# Revit family: console with cutout for bowl with tap hole
name_source: partatom
category: Furniture
units: mm (PartAtom-declared; Revit-internal decimal feet)

## family parameters
Always vertical = Yes
Cut with Voids When Loaded = No
OmniClass Number = 23.21.19.15.33.13
Room Calculation Point = No
Shared = Yes
Work Plane-Based = No

## types (40) — shared parameters
BIMOBJECT = Sanitary: Compound units
CATALOG = Hansgrohe
DESIGN = Germany
ETIM = EC011381 | Bathroom furniture set
IFC = Furnishing element
L1 = 140
MASTERFORMAT = 12 35 30.23 | Bathroom Casework
Manufacturer = Hansgrohe
NBSYN = $BASENUMBER.-$ARTNR.-$SURFACE.-$LODLEVEL.
NN = Console with cutout for bowl with tap hole
OBJECTTYPE = Object (single object)
OMNICLASS = 23-19 31 17 11 | Bathroom Units
PRODUCTFAMILY = Xelu Q
PRODUCTGROUP = console
PRODUCTURL = https://pro.hansgrohe.com
REGIONSET = Worldwide
UNICLASS2015 = Pr_40_20_76_94 | Vanity units
UNIFORMATII = E2010 | Fixed Furnishings
UNSPSC = 56 | Furniture and Furnishings

## per-type parameters (varying)
| type | ARTNR | BASENUMBER | GTINCODE | L | LINA | LL | LODLEVEL | Model | NAME | NB | PERMALINK | SPECIFICATION | SURFACE | WEIGHT |
| Console 1180_550 with cutout in the middle for bowl with tap hole-54122050-GLOSSY_WHITE-200 | 54122050 | Console 1180/550 with cutout in the middle for bowl with tap hole | 4059625457979 | 1180 | Console 1180/550 with cutout in the middle for bowl with tap hole-54122050-GLOSSY_WHITE-200 | 590 | 200 | Console 1180/550 with cutout in the middle for bowl with tap hole-54122050-GLOSSY_WHITE-200 | Xelu Q Console 1180/550 with cutout in the middle for bowl with tap hole | Console 1180/550 with cutout in the middle for bowl with tap hole-54122050-GLOSSY_WHITE-200 | 54122XXX | Surfaces:    - 54122050 High Gloss White  - 54122910 Diamond Matt Grey  - 54122230 Natural Oak  - 54122630 Dark Walnut      Specification: | GLOSSY_WHITE | 14.5 |
| Console 1180_550 with cutout in the middle for bowl with tap hole-54122050-GLOSSY_WHITE-400 | 54122050 | Console 1180/550 with cutout in the middle for bowl with tap hole | 4059625457979 | 1180 | Console 1180/550 with cutout in the middle for bowl with tap hole-54122050-GLOSSY_WHITE-400 | 590 | 400 | Console 1180/550 with cutout in the middle for bowl with tap hole-54122050-GLOSSY_WHITE-400 | Xelu Q Console 1180/550 with cutout in the middle for bowl with tap hole | Console 1180/550 with cutout in the middle for bowl with tap hole-54122050-GLOSSY_WHITE-400 | 54122XXX | Surfaces:    - 54122050 High Gloss White  - 54122910 Diamond Matt Grey  - 54122230 Natural Oak  - 54122630 Dark Walnut      Specification: | GLOSSY_WHITE | 14.5 |
| Console 1180_550 with cutout in the middle for bowl with tap hole-54122230-NATURAL_OAK-200 | 54122230 | Console 1180/550 with cutout in the middle for bowl with tap hole | 4059625457979 | 1180 | Console 1180/550 with cutout in the middle for bowl with tap hole-54122230-NATURAL_OAK-200 | 590 | 200 | Console 1180/550 with cutout in the middle for bowl with tap hole-54122230-NATURAL_OAK-200 | Xelu Q Console 1180/550 with cutout in the middle for bowl with tap hole | Console 1180/550 with cutout in the middle for bowl with tap hole-54122230-NATURAL_OAK-200 | 54122XXX | Surfaces:    - 54122050 High Gloss White  - 54122910 Diamond Matt Grey  - 54122230 Natural Oak  - 54122630 Dark Walnut      Specification: | NATURAL_OAK | 14.5 |
| Console 1180_550 with cutout in the middle for bowl with tap hole-54122230-NATURAL_OAK-400 | 54122230 | Console 1180/550 with cutout in the middle for bowl with tap hole | 4059625457979 | 1180 | Console 1180/550 with cutout in the middle for bowl with tap hole-54122230-NATURAL_OAK-400 | 590 | 400 | Console 1180/550 with cutout in the middle for bowl with tap hole-54122230-NATURAL_OAK-400 | Xelu Q Console 1180/550 with cutout in the middle for bowl with tap hole | Console 1180/550 with cutout in the middle for bowl with tap hole-54122230-NATURAL_OAK-400 | 54122XXX | Surfaces:    - 54122050 High Gloss White  - 54122910 Diamond Matt Grey  - 54122230 Natural Oak  - 54122630 Dark Walnut      Specification: | NATURAL_OAK | 14.5 |
| Console 1180_550 with cutout in the middle for bowl with tap hole-54122630-DARK_WALNUT-200 | 54122630 | Console 1180/550 with cutout in the middle for bowl with tap hole | 4059625457979 | 1180 | Console 1180/550 with cutout in the middle for bowl with tap hole-54122630-DARK_WALNUT-200 | 590 | 200 | Console 1180/550 with cutout in the middle for bowl with tap hole-54122630-DARK_WALNUT-200 | Xelu Q Console 1180/550 with cutout in the middle for bowl with tap hole | Console 1180/550 with cutout in the middle for bowl with tap hole-54122630-DARK_WALNUT-200 | 54122XXX | Surfaces:    - 54122050 High Gloss White  - 54122910 Diamond Matt Grey  - 54122230 Natural Oak  - 54122630 Dark Walnut      Specification: | DARK_WALNUT | 14.5 |
| Console 1180_550 with cutout in the middle for bowl with tap hole-54122630-DARK_WALNUT-400 | 54122630 | Console 1180/550 with cutout in the middle for bowl with tap hole | 4059625457979 | 1180 | Console 1180/550 with cutout in the middle for bowl with tap hole-54122630-DARK_WALNUT-400 | 590 | 400 | Console 1180/550 with cutout in the middle for bowl with tap hole-54122630-DARK_WALNUT-400 | Xelu Q Console 1180/550 with cutout in the middle for bowl with tap hole | Console 1180/550 with cutout in the middle for bowl with tap hole-54122630-DARK_WALNUT-400 | 54122XXX | Surfaces:    - 54122050 High Gloss White  - 54122910 Diamond Matt Grey  - 54122230 Natural Oak  - 54122630 Dark Walnut      Specification: | DARK_WALNUT | 14.5 |
| Console 1180_550 with cutout in the middle for bowl with tap hole-54122910-DIAMOND_GREY-200 | 54122910 | Console 1180/550 with cutout in the middle for bowl with tap hole | 4059625457979 | 1180 | Console 1180/550 with cutout in the middle for bowl with tap hole-54122910-DIAMOND_GREY-200 | 590 | 200 | Console 1180/550 with cutout in the middle for bowl with tap hole-54122910-DIAMOND_GREY-200 | Xelu Q Console 1180/550 with cutout in the middle for bowl with tap hole | Console 1180/550 with cutout in the middle for bowl with tap hole-54122910-DIAMOND_GREY-200 | 54122XXX | Surfaces:    - 54122050 High Gloss White  - 54122910 Diamond Matt Grey  - 54122230 Natural Oak  - 54122630 Dark Walnut      Specification: | DIAMOND_GREY | 14.5 |
| Console 1180_550 with cutout in the middle for bowl with tap hole-54122910-DIAMOND_GREY-400 | 54122910 | Console 1180/550 with cutout in the middle for bowl with tap hole | 4059625457979 | 1180 | Console 1180/550 with cutout in the middle for bowl with tap hole-54122910-DIAMOND_GREY-400 | 590 | 400 | Console 1180/550 with cutout in the middle for bowl with tap hole-54122910-DIAMOND_GREY-400 | Xelu Q Console 1180/550 with cutout in the middle for bowl with tap hole | Console 1180/550 with cutout in the middle for bowl with tap hole-54122910-DIAMOND_GREY-400 | 54122XXX | Surfaces:    - 54122050 High Gloss White  - 54122910 Diamond Matt Grey  - 54122230 Natural Oak  - 54122630 Dark Walnut      Specification: | DIAMOND_GREY | 14.5 |
| Console 1360_550 with cutout left for bowl with tap hole-54123050-GLOSSY_WHITE-200 | 54123050 | Console 1360/550 with cutout left for bowl with tap hole | 4059625457931 | 1360 | Console 1360/550 with cutout left for bowl with tap hole-54123050-GLOSSY_WHITE-200 | 340 | 200 | Console 1360/550 with cutout left for bowl with tap hole-54123050-GLOSSY_WHITE-200 | Xelu Q Console 1360/550 with cutout left for bowl with tap hole | Console 1360/550 with cutout left for bowl with tap hole-54123050-GLOSSY_WHITE-200 | 54123XXX | Surfaces:    - 54123050 High Gloss White  - 54123910 Diamond Matt Grey  - 54123230 Natural Oak  - 54123630 Dark Walnut      Specification: | GLOSSY_WHITE | 12.2 |
| Console 1360_550 with cutout left for bowl with tap hole-54123050-GLOSSY_WHITE-400 | 54123050 | Console 1360/550 with cutout left for bowl with tap hole | 4059625457931 | 1360 | Console 1360/550 with cutout left for bowl with tap hole-54123050-GLOSSY_WHITE-400 | 340 | 400 | Console 1360/550 with cutout left for bowl with tap hole-54123050-GLOSSY_WHITE-400 | Xelu Q Console 1360/550 with cutout left for bowl with tap hole | Console 1360/550 with cutout left for bowl with tap hole-54123050-GLOSSY_WHITE-400 | 54123XXX | Surfaces:    - 54123050 High Gloss White  - 54123910 Diamond Matt Grey  - 54123230 Natural Oak  - 54123630 Dark Walnut      Specification: | GLOSSY_WHITE | 12.2 |
| Console 1360_550 with cutout left for bowl with tap hole-54123230-NATURAL_OAK-200 | 54123230 | Console 1360/550 with cutout left for bowl with tap hole | 4059625457931 | 1360 | Console 1360/550 with cutout left for bowl with tap hole-54123230-NATURAL_OAK-200 | 340 | 200 | Console 1360/550 with cutout left for bowl with tap hole-54123230-NATURAL_OAK-200 | Xelu Q Console 1360/550 with cutout left for bowl with tap hole | Console 1360/550 with cutout left for bowl with tap hole-54123230-NATURAL_OAK-200 | 54123XXX | Surfaces:    - 54123050 High Gloss White  - 54123910 Diamond Matt Grey  - 54123230 Natural Oak  - 54123630 Dark Walnut      Specification: | NATURAL_OAK | 12.2 |
| Console 1360_550 with cutout left for bowl with tap hole-54123230-NATURAL_OAK-400 | 54123230 | Console 1360/550 with cutout left for bowl with tap hole | 4059625457931 | 1360 | Console 1360/550 with cutout left for bowl with tap hole-54123230-NATURAL_OAK-400 | 340 | 400 | Console 1360/550 with cutout left for bowl with tap hole-54123230-NATURAL_OAK-400 | Xelu Q Console 1360/550 with cutout left for bowl with tap hole | Console 1360/550 with cutout left for bowl with tap hole-54123230-NATURAL_OAK-400 | 54123XXX | Surfaces:    - 54123050 High Gloss White  - 54123910 Diamond Matt Grey  - 54123230 Natural Oak  - 54123630 Dark Walnut      Specification: | NATURAL_OAK | 12.2 |
| Console 1360_550 with cutout left for bowl with tap hole-54123630-DIAMOND_GREY-200 | 54123630 | Console 1360/550 with cutout left for bowl with tap hole | 4059625457931 | 1360 | Console 1360/550 with cutout left for bowl with tap hole-54123630-DIAMOND_GREY-200 | 340 | 200 | Console 1360/550 with cutout left for bowl with tap hole-54123630-DIAMOND_GREY-200 | Xelu Q Console 1360/550 with cutout left for bowl with tap hole | Console 1360/550 with cutout left for bowl with tap hole-54123630-DIAMOND_GREY-200 | 54123XXX | Surfaces:    - 54123050 High Gloss White  - 54123910 Diamond Matt Grey  - 54123230 Natural Oak  - 54123630 Dark Walnut      Specification: | DIAMOND_GREY | 12.2 |
| Console 1360_550 with cutout left for bowl with tap hole-54123630-DIAMOND_GREY-400 | 54123630 | Console 1360/550 with cutout left for bowl with tap hole | 4059625457931 | 1360 | Console 1360/550 with cutout left for bowl with tap hole-54123630-DIAMOND_GREY-400 | 340 | 400 | Console 1360/550 with cutout left for bowl with tap hole-54123630-DIAMOND_GREY-400 | Xelu Q Console 1360/550 with cutout left for bowl with tap hole | Console 1360/550 with cutout left for bowl with tap hole-54123630-DIAMOND_GREY-400 | 54123XXX | Surfaces:    - 54123050 High Gloss White  - 54123910 Diamond Matt Grey  - 54123230 Natural Oak  - 54123630 Dark Walnut      Specification: | DIAMOND_GREY | 12.2 |
| Console 1360_550 with cutout left for bowl with tap hole-54123910-DARK_WALNUT-200 | 54123910 | Console 1360/550 with cutout left for bowl with tap hole | 4059625457931 | 1360 | Console 1360/550 with cutout left for bowl with tap hole-54123910-DARK_WALNUT-200 | 340 | 200 | Console 1360/550 with cutout left for bowl with tap hole-54123910-DARK_WALNUT-200 | Xelu Q Console 1360/550 with cutout left for bowl with tap hole | Console 1360/550 with cutout left for bowl with tap hole-54123910-DARK_WALNUT-200 | 54123XXX | Surfaces:    - 54123050 High Gloss White  - 54123910 Diamond Matt Grey  - 54123230 Natural Oak  - 54123630 Dark Walnut      Specification: | DARK_WALNUT | 12.2 |
| Console 1360_550 with cutout left for bowl with tap hole-54123910-DARK_WALNUT-400 | 54123910 | Console 1360/550 with cutout left for bowl with tap hole | 4059625457931 | 1360 | Console 1360/550 with cutout left for bowl with tap hole-54123910-DARK_WALNUT-400 | 340 | 400 | Console 1360/550 with cutout left for bowl with tap hole-54123910-DARK_WALNUT-400 | Xelu Q Console 1360/550 with cutout left for bowl with tap hole | Console 1360/550 with cutout left for bowl with tap hole-54123910-DARK_WALNUT-400 | 54123XXX | Surfaces:    - 54123050 High Gloss White  - 54123910 Diamond Matt Grey  - 54123230 Natural Oak  - 54123630 Dark Walnut      Specification: | DARK_WALNUT | 12.2 |
| Console 1360_550 with cutout right for bowl with tap hole-54124050-NATURAL_OAK-200 | 54124050 | Console 1360/550 with cutout right for bowl with tap hole | 4059625457894 | 1360 | Console 1360/550 with cutout right for bowl with tap hole-54124050-NATURAL_OAK-200 | 1020 | 200 | Console 1360/550 with cutout right for bowl with tap hole-54124050-NATURAL_OAK-200 | Xelu Q Console 1360/550 with cutout right for bowl with tap hole | Console 1360/550 with cutout right for bowl with tap hole-54124050-NATURAL_OAK-200 | 54124XXX | Surfaces:    - 54124050 High Gloss White  - 54124910 Diamond Matt Grey  - 54124230 Natural Oak  - 54124630 Dark Walnut      Specification: | NATURAL_OAK | 12.2 |
| Console 1360_550 with cutout right for bowl with tap hole-54124050-NATURAL_OAK-400 | 54124050 | Console 1360/550 with cutout right for bowl with tap hole | 4059625457894 | 1360 | Console 1360/550 with cutout right for bowl with tap hole-54124050-NATURAL_OAK-400 | 1020 | 400 | Console 1360/550 with cutout right for bowl with tap hole-54124050-NATURAL_OAK-400 | Xelu Q Console 1360/550 with cutout right for bowl with tap hole | Console 1360/550 with cutout right for bowl with tap hole-54124050-NATURAL_OAK-400 | 54124XXX | Surfaces:    - 54124050 High Gloss White  - 54124910 Diamond Matt Grey  - 54124230 Natural Oak  - 54124630 Dark Walnut      Specification: | NATURAL_OAK | 12.2 |
| Console 1360_550 with cutout right for bowl with tap hole-54124230-DIAMOND_GREY-200 | 54124230 | Console 1360/550 with cutout right for bowl with tap hole | 4059625457894 | 1360 | Console 1360/550 with cutout right for bowl with tap hole-54124230-DIAMOND_GREY-200 | 1020 | 200 | Console 1360/550 with cutout right for bowl with tap hole-54124230-DIAMOND_GREY-200 | Xelu Q Console 1360/550 with cutout right for bowl with tap hole | Console 1360/550 with cutout right for bowl with tap hole-54124230-DIAMOND_GREY-200 | 54124XXX | Surfaces:    - 54124050 High Gloss White  - 54124910 Diamond Matt Grey  - 54124230 Natural Oak  - 54124630 Dark Walnut      Specification: | DIAMOND_GREY | 12.2 |
| Console 1360_550 with cutout right for bowl with tap hole-54124230-DIAMOND_GREY-400 | 54124230 | Console 1360/550 with cutout right for bowl with tap hole | 4059625457894 | 1360 | Console 1360/550 with cutout right for bowl with tap hole-54124230-DIAMOND_GREY-400 | 1020 | 400 | Console 1360/550 with cutout right for bowl with tap hole-54124230-DIAMOND_GREY-400 | Xelu Q Console 1360/550 with cutout right for bowl with tap hole | Console 1360/550 with cutout right for bowl with tap hole-54124230-DIAMOND_GREY-400 | 54124XXX | Surfaces:    - 54124050 High Gloss White  - 54124910 Diamond Matt Grey  - 54124230 Natural Oak  - 54124630 Dark Walnut      Specification: | DIAMOND_GREY | 12.2 |
| Console 1360_550 with cutout right for bowl with tap hole-54124630-DARK_WALNUT-200 | 54124630 | Console 1360/550 with cutout right for bowl with tap hole | 4059625457894 | 1360 | Console 1360/550 with cutout right for bowl with tap hole-54124630-DARK_WALNUT-200 | 1020 | 200 | Console 1360/550 with cutout right for bowl with tap hole-54124630-DARK_WALNUT-200 | Xelu Q Console 1360/550 with cutout right for bowl with tap hole | Console 1360/550 with cutout right for bowl with tap hole-54124630-DARK_WALNUT-200 | 54124XXX | Surfaces:    - 54124050 High Gloss White  - 54124910 Diamond Matt Grey  - 54124230 Natural Oak  - 54124630 Dark Walnut      Specification: | DARK_WALNUT | 12.2 |
| Console 1360_550 with cutout right for bowl with tap hole-54124630-DARK_WALNUT-400 | 54124630 | Console 1360/550 with cutout right for bowl with tap hole | 4059625457894 | 1360 | Console 1360/550 with cutout right for bowl with tap hole-54124630-DARK_WALNUT-400 | 1020 | 400 | Console 1360/550 with cutout right for bowl with tap hole-54124630-DARK_WALNUT-400 | Xelu Q Console 1360/550 with cutout right for bowl with tap hole | Console 1360/550 with cutout right for bowl with tap hole-54124630-DARK_WALNUT-400 | 54124XXX | Surfaces:    - 54124050 High Gloss White  - 54124910 Diamond Matt Grey  - 54124230 Natural Oak  - 54124630 Dark Walnut      Specification: | DARK_WALNUT | 12.2 |
| Console 1360_550 with cutout right for bowl with tap hole-54124910-GLOSSY_WHITE-200 | 54124910 | Console 1360/550 with cutout right for bowl with tap hole | 4059625457894 | 1360 | Console 1360/550 with cutout right for bowl with tap hole-54124910-GLOSSY_WHITE-200 | 1020 | 200 | Console 1360/550 with cutout right for bowl with tap hole-54124910-GLOSSY_WHITE-200 | Xelu Q Console 1360/550 with cutout right for bowl with tap hole | Console 1360/550 with cutout right for bowl with tap hole-54124910-GLOSSY_WHITE-200 | 54124XXX | Surfaces:    - 54124050 High Gloss White  - 54124910 Diamond Matt Grey  - 54124230 Natural Oak  - 54124630 Dark Walnut      Specification: | GLOSSY_WHITE | 12.2 |
| Console 1360_550 with cutout right for bowl with tap hole-54124910-GLOSSY_WHITE-400 | 54124910 | Console 1360/550 with cutout right for bowl with tap hole | 4059625457894 | 1360 | Console 1360/550 with cutout right for bowl with tap hole-54124910-GLOSSY_WHITE-400 | 1020 | 400 | Console 1360/550 with cutout right for bowl with tap hole-54124910-GLOSSY_WHITE-400 | Xelu Q Console 1360/550 with cutout right for bowl with tap hole | Console 1360/550 with cutout right for bowl with tap hole-54124910-GLOSSY_WHITE-400 | 54124XXX | Surfaces:    - 54124050 High Gloss White  - 54124910 Diamond Matt Grey  - 54124230 Natural Oak  - 54124630 Dark Walnut      Specification: | GLOSSY_WHITE | 12.2 |
| Console 780_550 with cutout in the middle for bowls with tap hole-54120050-DARK_WALNUT-200 | 54120050 | Console 780/550 with cutout in the middle for bowls with tap hole | 4059625457658 | 780 | Console 780/550 with cutout in the middle for bowls with tap hole-54120050-DARK_WALNUT-200 | 390 | 200 | Console 780/550 with cutout in the middle for bowls with tap hole-54120050-DARK_WALNUT-200 | Xelu Q Console 780/550 with cutout in the middle for bowls with tap hole | Console 780/550 with cutout in the middle for bowls with tap hole-54120050-DARK_WALNUT-200 | 54120XXX | Surfaces:    - 54120050 High Gloss White  - 54120910 Diamond Matt Grey  - 54120230 Natural Oak  - 54120630 Dark Walnut      Specification: | DARK_WALNUT | 8.4 |
| Console 780_550 with cutout in the middle for bowls with tap hole-54120050-DARK_WALNUT-400 | 54120050 | Console 780/550 with cutout in the middle for bowls with tap hole | 4059625457658 | 780 | Console 780/550 with cutout in the middle for bowls with tap hole-54120050-DARK_WALNUT-400 | 390 | 400 | Console 780/550 with cutout in the middle for bowls with tap hole-54120050-DARK_WALNUT-400 | Xelu Q Console 780/550 with cutout in the middle for bowls with tap hole | Console 780/550 with cutout in the middle for bowls with tap hole-54120050-DARK_WALNUT-400 | 54120XXX | Surfaces:    - 54120050 High Gloss White  - 54120910 Diamond Matt Grey  - 54120230 Natural Oak  - 54120630 Dark Walnut      Specification: | DARK_WALNUT | 8.4 |
| Console 780_550 with cutout in the middle for bowls with tap hole-54120230-DIAMOND_GREY-200 | 54120230 | Console 780/550 with cutout in the middle for bowls with tap hole | 4059625457658 | 780 | Console 780/550 with cutout in the middle for bowls with tap hole-54120230-DIAMOND_GREY-200 | 390 | 200 | Console 780/550 with cutout in the middle for bowls with tap hole-54120230-DIAMOND_GREY-200 | Xelu Q Console 780/550 with cutout in the middle for bowls with tap hole | Console 780/550 with cutout in the middle for bowls with tap hole-54120230-DIAMOND_GREY-200 | 54120XXX | Surfaces:    - 54120050 High Gloss White  - 54120910 Diamond Matt Grey  - 54120230 Natural Oak  - 54120630 Dark Walnut      Specification: | DIAMOND_GREY | 8.4 |
| Console 780_550 with cutout in the middle for bowls with tap hole-54120230-DIAMOND_GREY-400 | 54120230 | Console 780/550 with cutout in the middle for bowls with tap hole | 4059625457658 | 780 | Console 780/550 with cutout in the middle for bowls with tap hole-54120230-DIAMOND_GREY-400 | 390 | 400 | Console 780/550 with cutout in the middle for bowls with tap hole-54120230-DIAMOND_GREY-400 | Xelu Q Console 780/550 with cutout in the middle for bowls with tap hole | Console 780/550 with cutout in the middle for bowls with tap hole-54120230-DIAMOND_GREY-400 | 54120XXX | Surfaces:    - 54120050 High Gloss White  - 54120910 Diamond Matt Grey  - 54120230 Natural Oak  - 54120630 Dark Walnut      Specification: | DIAMOND_GREY | 8.4 |
| Console 780_550 with cutout in the middle for bowls with tap hole-54120630-NATURAL_OAK-200 | 54120630 | Console 780/550 with cutout in the middle for bowls with tap hole | 4059625457658 | 780 | Console 780/550 with cutout in the middle for bowls with tap hole-54120630-NATURAL_OAK-200 | 390 | 200 | Console 780/550 with cutout in the middle for bowls with tap hole-54120630-NATURAL_OAK-200 | Xelu Q Console 780/550 with cutout in the middle for bowls with tap hole | Console 780/550 with cutout in the middle for bowls with tap hole-54120630-NATURAL_OAK-200 | 54120XXX | Surfaces:    - 54120050 High Gloss White  - 54120910 Diamond Matt Grey  - 54120230 Natural Oak  - 54120630 Dark Walnut      Specification: | NATURAL_OAK | 8.4 |
| Console 780_550 with cutout in the middle for bowls with tap hole-54120630-NATURAL_OAK-400 | 54120630 | Console 780/550 with cutout in the middle for bowls with tap hole | 4059625457658 | 780 | Console 780/550 with cutout in the middle for bowls with tap hole-54120630-NATURAL_OAK-400 | 390 | 400 | Console 780/550 with cutout in the middle for bowls with tap hole-54120630-NATURAL_OAK-400 | Xelu Q Console 780/550 with cutout in the middle for bowls with tap hole | Console 780/550 with cutout in the middle for bowls with tap hole-54120630-NATURAL_OAK-400 | 54120XXX | Surfaces:    - 54120050 High Gloss White  - 54120910 Diamond Matt Grey  - 54120230 Natural Oak  - 54120630 Dark Walnut      Specification: | NATURAL_OAK | 8.4 |
| Console 780_550 with cutout in the middle for bowls with tap hole-54120910-GLOSSY_WHITE-200 | 54120910 | Console 780/550 with cutout in the middle for bowls with tap hole | 4059625457658 | 780 | Console 780/550 with cutout in the middle for bowls with tap hole-54120910-GLOSSY_WHITE-200 | 390 | 200 | Console 780/550 with cutout in the middle for bowls with tap hole-54120910-GLOSSY_WHITE-200 | Xelu Q Console 780/550 with cutout in the middle for bowls with tap hole | Console 780/550 with cutout in the middle for bowls with tap hole-54120910-GLOSSY_WHITE-200 | 54120XXX | Surfaces:    - 54120050 High Gloss White  - 54120910 Diamond Matt Grey  - 54120230 Natural Oak  - 54120630 Dark Walnut      Specification: | GLOSSY_WHITE | 8.4 |
| Console 780_550 with cutout in the middle for bowls with tap hole-54120910-GLOSSY_WHITE-400 | 54120910 | Console 780/550 with cutout in the middle for bowls with tap hole | 4059625457658 | 780 | Console 780/550 with cutout in the middle for bowls with tap hole-54120910-GLOSSY_WHITE-400 | 390 | 400 | Console 780/550 with cutout in the middle for bowls with tap hole-54120910-GLOSSY_WHITE-400 | Xelu Q Console 780/550 with cutout in the middle for bowls with tap hole | Console 780/550 with cutout in the middle for bowls with tap hole-54120910-GLOSSY_WHITE-400 | 54120XXX | Surfaces:    - 54120050 High Gloss White  - 54120910 Diamond Matt Grey  - 54120230 Natural Oak  - 54120630 Dark Walnut      Specification: | GLOSSY_WHITE | 8.4 |
| Console 980_550 with cutout in the middle for bowl with tap hole-54121050-NATURAL_OAK-200 | 54121050 | Console 980/550 with cutout in the middle for bowl with tap hole | 4059625458013 | 980 | Console 980/550 with cutout in the middle for bowl with tap hole-54121050-NATURAL_OAK-200 | 490 | 200 | Console 980/550 with cutout in the middle for bowl with tap hole-54121050-NATURAL_OAK-200 | Xelu Q Console 980/550 with cutout in the middle for bowl with tap hole | Console 980/550 with cutout in the middle for bowl with tap hole-54121050-NATURAL_OAK-200 | 54121XXX | Surfaces:    - 54121050 High Gloss White  - 54121910 Diamond Matt Grey  - 54121230 Natural Oak  - 54121630 Dark Walnut      Specification: | NATURAL_OAK | 13.2 |
| Console 980_550 with cutout in the middle for bowl with tap hole-54121050-NATURAL_OAK-400 | 54121050 | Console 980/550 with cutout in the middle for bowl with tap hole | 4059625458013 | 980 | Console 980/550 with cutout in the middle for bowl with tap hole-54121050-NATURAL_OAK-400 | 490 | 400 | Console 980/550 with cutout in the middle for bowl with tap hole-54121050-NATURAL_OAK-400 | Xelu Q Console 980/550 with cutout in the middle for bowl with tap hole | Console 980/550 with cutout in the middle for bowl with tap hole-54121050-NATURAL_OAK-400 | 54121XXX | Surfaces:    - 54121050 High Gloss White  - 54121910 Diamond Matt Grey  - 54121230 Natural Oak  - 54121630 Dark Walnut      Specification: | NATURAL_OAK | 13.2 |
| Console 980_550 with cutout in the middle for bowl with tap hole-54121230-GLOSSY_WHITE-200 | 54121230 | Console 980/550 with cutout in the middle for bowl with tap hole | 4059625458013 | 980 | Console 980/550 with cutout in the middle for bowl with tap hole-54121230-GLOSSY_WHITE-200 | 490 | 200 | Console 980/550 with cutout in the middle for bowl with tap hole-54121230-GLOSSY_WHITE-200 | Xelu Q Console 980/550 with cutout in the middle for bowl with tap hole | Console 980/550 with cutout in the middle for bowl with tap hole-54121230-GLOSSY_WHITE-200 | 54121XXX | Surfaces:    - 54121050 High Gloss White  - 54121910 Diamond Matt Grey  - 54121230 Natural Oak  - 54121630 Dark Walnut      Specification: | GLOSSY_WHITE | 13.2 |
| Console 980_550 with cutout in the middle for bowl with tap hole-54121230-GLOSSY_WHITE-400 | 54121230 | Console 980/550 with cutout in the middle for bowl with tap hole | 4059625458013 | 980 | Console 980/550 with cutout in the middle for bowl with tap hole-54121230-GLOSSY_WHITE-400 | 490 | 400 | Console 980/550 with cutout in the middle for bowl with tap hole-54121230-GLOSSY_WHITE-400 | Xelu Q Console 980/550 with cutout in the middle for bowl with tap hole | Console 980/550 with cutout in the middle for bowl with tap hole-54121230-GLOSSY_WHITE-400 | 54121XXX | Surfaces:    - 54121050 High Gloss White  - 54121910 Diamond Matt Grey  - 54121230 Natural Oak  - 54121630 Dark Walnut      Specification: | GLOSSY_WHITE | 13.2 |
| Console 980_550 with cutout in the middle for bowl with tap hole-54121630-DARK_WALNUT-200 | 54121630 | Console 980/550 with cutout in the middle for bowl with tap hole | 4059625458013 | 980 | Console 980/550 with cutout in the middle for bowl with tap hole-54121630-DARK_WALNUT-200 | 490 | 200 | Console 980/550 with cutout in the middle for bowl with tap hole-54121630-DARK_WALNUT-200 | Xelu Q Console 980/550 with cutout in the middle for bowl with tap hole | Console 980/550 with cutout in the middle for bowl with tap hole-54121630-DARK_WALNUT-200 | 54121XXX | Surfaces:    - 54121050 High Gloss White  - 54121910 Diamond Matt Grey  - 54121230 Natural Oak  - 54121630 Dark Walnut      Specification: | DARK_WALNUT | 13.2 |
| Console 980_550 with cutout in the middle for bowl with tap hole-54121630-DARK_WALNUT-400 | 54121630 | Console 980/550 with cutout in the middle for bowl with tap hole | 4059625458013 | 980 | Console 980/550 with cutout in the middle for bowl with tap hole-54121630-DARK_WALNUT-400 | 490 | 400 | Console 980/550 with cutout in the middle for bowl with tap hole-54121630-DARK_WALNUT-400 | Xelu Q Console 980/550 with cutout in the middle for bowl with tap hole | Console 980/550 with cutout in the middle for bowl with tap hole-54121630-DARK_WALNUT-400 | 54121XXX | Surfaces:    - 54121050 High Gloss White  - 54121910 Diamond Matt Grey  - 54121230 Natural Oak  - 54121630 Dark Walnut      Specification: | DARK_WALNUT | 13.2 |
| Console 980_550 with cutout in the middle for bowl with tap hole-54121910-DIAMOND_GREY-200 | 54121910 | Console 980/550 with cutout in the middle for bowl with tap hole | 4059625458013 | 980 | Console 980/550 with cutout in the middle for bowl with tap hole-54121910-DIAMOND_GREY-200 | 490 | 200 | Console 980/550 with cutout in the middle for bowl with tap hole-54121910-DIAMOND_GREY-200 | Xelu Q Console 980/550 with cutout in the middle for bowl with tap hole | Console 980/550 with cutout in the middle for bowl with tap hole-54121910-DIAMOND_GREY-200 | 54121XXX | Surfaces:    - 54121050 High Gloss White  - 54121910 Diamond Matt Grey  - 54121230 Natural Oak  - 54121630 Dark Walnut      Specification: | DIAMOND_GREY | 13.2 |
| Console 980_550 with cutout in the middle for bowl with tap hole-54121910-DIAMOND_GREY-400 | 54121910 | Console 980/550 with cutout in the middle for bowl with tap hole | 4059625458013 | 980 | Console 980/550 with cutout in the middle for bowl with tap hole-54121910-DIAMOND_GREY-400 | 490 | 400 | Console 980/550 with cutout in the middle for bowl with tap hole-54121910-DIAMOND_GREY-400 | Xelu Q Console 980/550 with cutout in the middle for bowl with tap hole | Console 980/550 with cutout in the middle for bowl with tap hole-54121910-DIAMOND_GREY-400 | 54121XXX | Surfaces:    - 54121050 High Gloss White  - 54121910 Diamond Matt Grey  - 54121230 Natural Oak  - 54121630 Dark Walnut      Specification: | DIAMOND_GREY | 13.2 |

type visibility flags: 40 boolean params named "<type name>_RX0RY0RZ0TX0TY0TZ0_V" — each type sets only its own to Yes (folded from table)

## geometry (parser evidence)
native form markers: Sweep x97
no freeform markers — native parametric forms only
